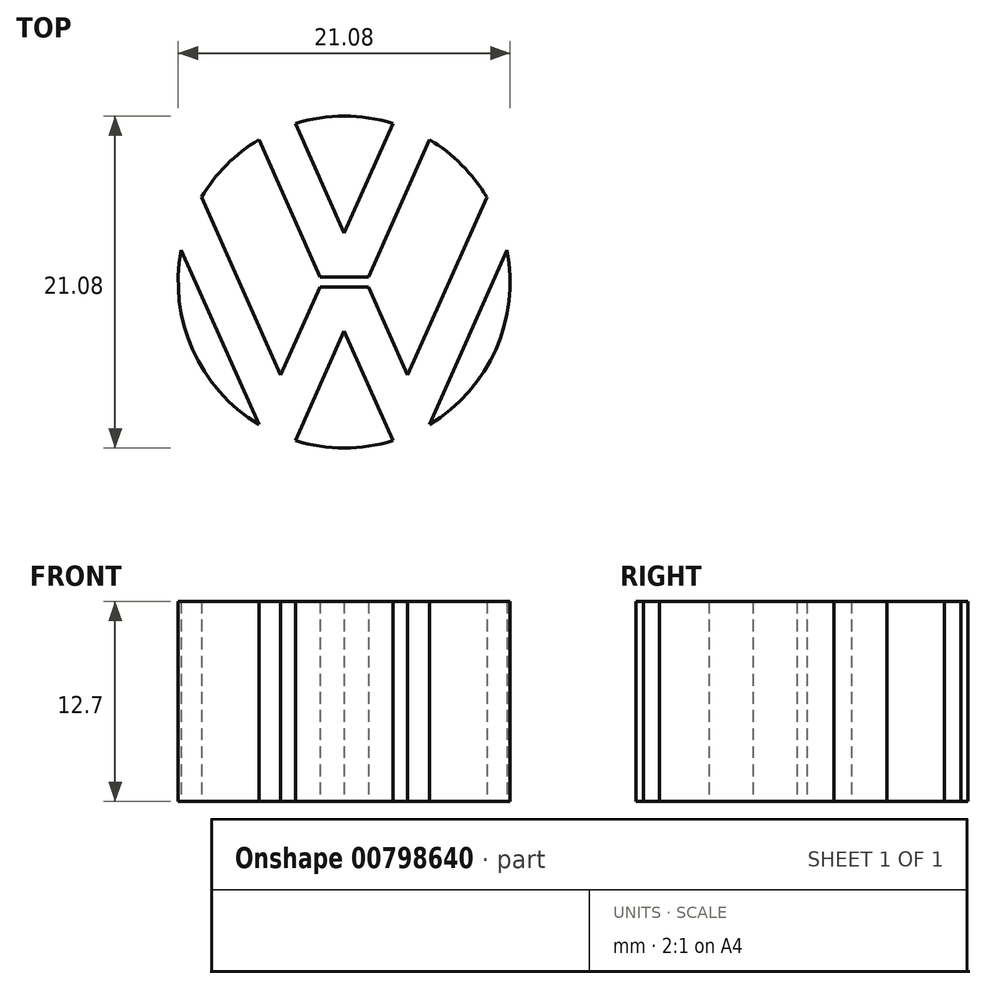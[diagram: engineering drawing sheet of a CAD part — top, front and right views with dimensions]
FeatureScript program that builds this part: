
annotation { "Feature Type Name" : "Feature", "Feature Type Description" : "" }
export const myFeature = defineFeature(function(context is Context, id is Id, definition is map)
    precondition{}
    {
        {
            var Q0;
            Q0=qCreatedBy(makeId("Top.planeOp"),FACE);
            var sketch = newSketch(context, id + "F0", { "sketchPlane" : qUnion([Q0])});
            skCircle(sketch, "E0", {"center": v(0, 0) * mm, "radius": 12.7 * mm});
            skArc(sketch, "E1.0", {"start": v(-5.42, 9.04) * mm, "mid": v(-7.47, 7.44) * mm, "end": v(-9.06, 5.39) * mm});
            skLineSegment(sketch, "E2", {"start": v(0, 14.76) * mm, "end": v(0, -15.86) * mm});
            skLineSegment(sketch, "E3.0", {"start": v(1.53, 0.32) * mm, "end": v(5.42, 9.04) * mm});
            skLineSegment(sketch, "E3.1", {"start": v(0, -3.12) * mm, "end": v(-3.1, -10.08) * mm});
            skLineSegment(sketch, "E4.0", {"start": v(0, 3.12) * mm, "end": v(3.1, 10.08) * mm});
            skLineSegment(sketch, "E4.1", {"start": v(-1.53, -0.32) * mm, "end": v(-4.03, -5.92) * mm});
            skLineSegment(sketch, "E5.0", {"start": v(0, 3.12) * mm, "end": v(-3.1, 10.08) * mm});
            skLineSegment(sketch, "E5.1", {"start": v(1.53, -0.32) * mm, "end": v(4.03, -5.92) * mm});
            skLineSegment(sketch, "E6.0", {"start": v(-1.53, 0.32) * mm, "end": v(-5.42, 9.04) * mm});
            skLineSegment(sketch, "E6.1", {"start": v(0, -3.12) * mm, "end": v(3.1, -10.08) * mm});
            skLineSegment(sketch, "E7", {"start": v(5.42, -9.04) * mm, "end": v(10.34, 2.03) * mm});
            skLineSegment(sketch, "E8", {"start": v(-5.42, -9.04) * mm, "end": v(-10.34, 2.03) * mm});
            skLineSegment(sketch, "E9.0", {"start": v(-4.03, -5.92) * mm, "end": v(-9.06, 5.39) * mm});
            skLineSegment(sketch, "E10.0", {"start": v(4.03, -5.92) * mm, "end": v(9.06, 5.39) * mm});
            skArc(sketch, "E11.trimOffspring", {"start": v(-10.34, 2.03) * mm, "mid": v(-9.63, -4.29) * mm, "end": v(-5.42, -9.04) * mm});
            skArc(sketch, "E12.trimOffspring", {"start": v(-3.1, -10.08) * mm, "mid": v(0, -10.54) * mm, "end": v(3.1, -10.08) * mm});
            skArc(sketch, "E13.trimOffspring", {"start": v(5.42, -9.04) * mm, "mid": v(9.63, -4.29) * mm, "end": v(10.34, 2.03) * mm});
            skArc(sketch, "E14.trimOffspring", {"start": v(9.06, 5.39) * mm, "mid": v(7.47, 7.44) * mm, "end": v(5.42, 9.04) * mm});
            skArc(sketch, "E15.trimOffspring", {"start": v(3.1, 10.08) * mm, "mid": v(0, 10.54) * mm, "end": v(-3.1, 10.08) * mm});
            skLineSegment(sketch, "E16.0", {"start": v(-1.53, -0.32) * mm, "end": v(1.53, -0.32) * mm});
            skLineSegment(sketch, "E17.0", {"start": v(-1.53, 0.32) * mm, "end": v(1.53, 0.32) * mm});
            skSolve(sketch);
        }
        {
            var Q0;
            Q0=makeQuery(id+"F0.imprint","IMPRINT",FACE,{"disambiguationData":[TD([[makeQuery(id+"F0.imprint","IMPRINT",EDGE,{"derivedFrom":sQuery(id+"F0.wireOp",EDGE,"E1.0")}),1.0]])]});
            var Q1;
            {var subQ0=sQuery(id+"F0.wireOp",EDGE,"E5.0");Q1=makeQuery(id+"F0.imprint","IMPRINT",FACE,{"disambiguationData":[TD([[makeQuery(id+"F0.imprint","IMPRINT",EDGE,{"derivedFrom":subQ0}),-1.0]])]});}
            var Q2;
            {var subQ1=sQuery(id+"F0.wireOp",EDGE,"E3.0");Q2=makeQuery(id+"F0.imprint","IMPRINT",FACE,{"disambiguationData":[TD([[makeQuery(id+"F0.imprint","IMPRINT",EDGE,{"derivedFrom":subQ1}),-1.0]])]});}
            var Q3;
            Q3=makeQuery(id+"F0.imprint","IMPRINT",FACE,{"disambiguationData":[TD([[makeQuery(id+"F0.imprint","IMPRINT",EDGE,{"derivedFrom":sQuery(id+"F0.wireOp",EDGE,"E7")}),-1.0]])]});
            var Q4;
            {var subQ0=sQuery(id+"F0.wireOp",EDGE,"E6.1");Q4=makeQuery(id+"F0.imprint","IMPRINT",FACE,{"disambiguationData":[TD([[makeQuery(id+"F0.imprint","IMPRINT",EDGE,{"derivedFrom":subQ0}),-1.0]])]});}
            var Q5;
            {var subQ0=sQuery(id+"F0.wireOp",EDGE,"E3.1");Q5=makeQuery(id+"F0.imprint","IMPRINT",FACE,{"disambiguationData":[TD([[makeQuery(id+"F0.imprint","IMPRINT",EDGE,{"derivedFrom":subQ0}),1.0]])]});}
            var Q6;
            Q6=makeQuery(id+"F0.imprint","IMPRINT",FACE,{"disambiguationData":[TD([[makeQuery(id+"F0.imprint","IMPRINT",EDGE,{"derivedFrom":sQuery(id+"F0.wireOp",EDGE,"E8")}),1.0]])]});
            var Q7;
            {var subQ0=sQuery(id+"F0.wireOp",EDGE,"E4.0");Q7=makeQuery(id+"F0.imprint","IMPRINT",FACE,{"disambiguationData":[TD([[makeQuery(id+"F0.imprint","IMPRINT",EDGE,{"derivedFrom":subQ0}),1.0]])]});}
            extrude(context, id + "F1", {"entities" : qUnion([Q0, Q1, Q2, Q3, Q4, Q5, Q6, Q7]), "depth" : 12.7 * mm, "offsetDistance" : 25.4 * mm});
        }
    });
